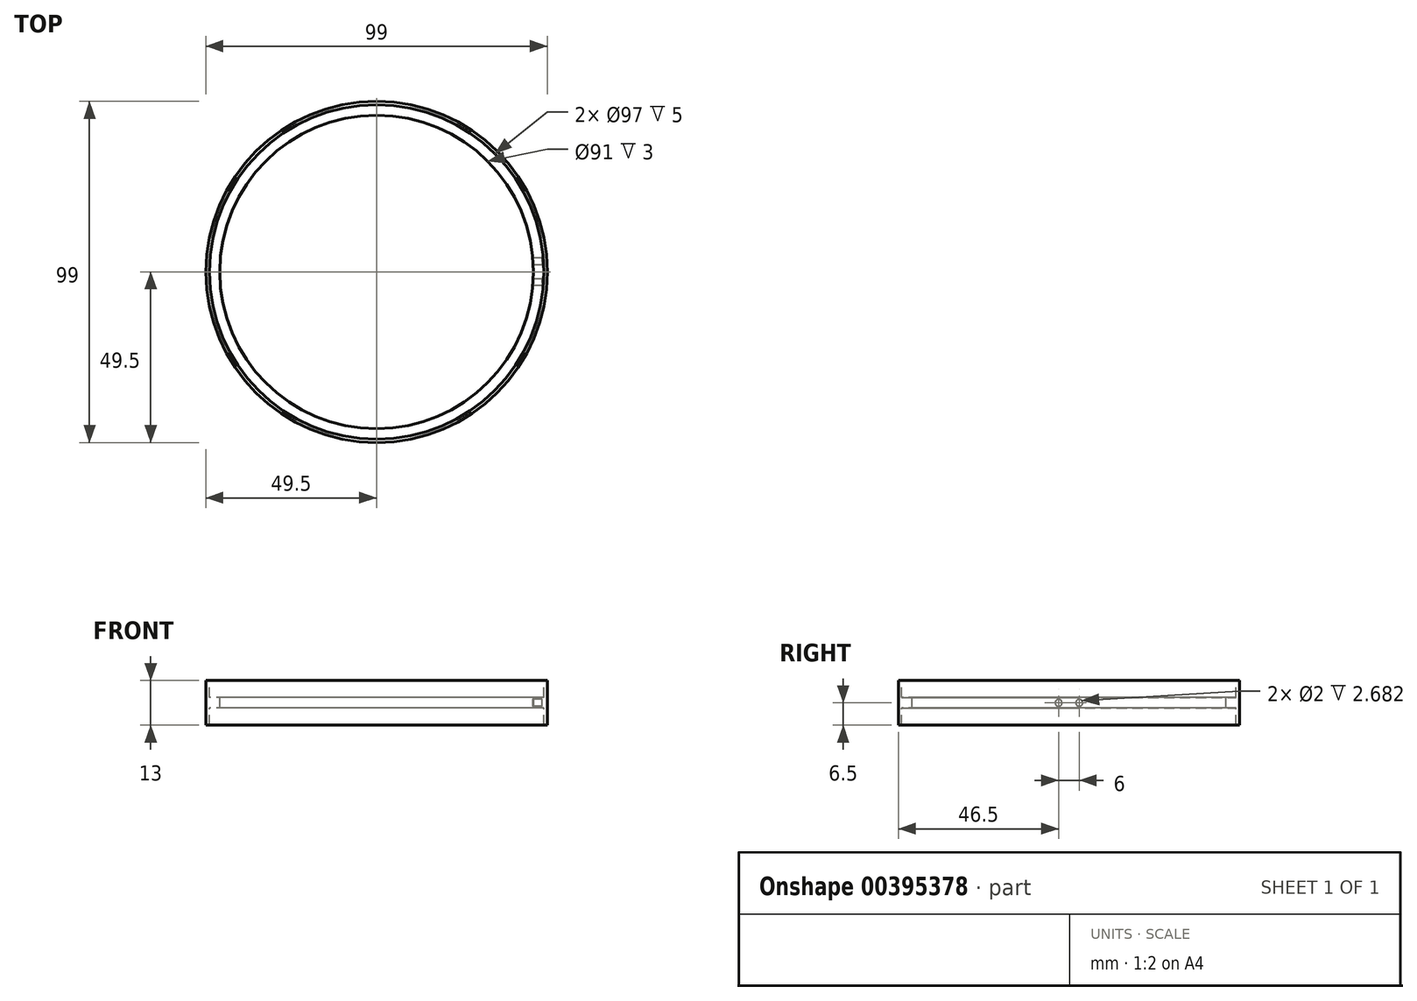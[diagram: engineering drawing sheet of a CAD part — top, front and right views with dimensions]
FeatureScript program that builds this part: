
annotation { "Feature Type Name" : "Feature", "Feature Type Description" : "" }
export const myFeature = defineFeature(function(context is Context, id is Id, definition is map)
    precondition{}
    {
        {
            var Q0;
            Q0=qCreatedBy(makeId("Front.planeOp"),FACE);
            var sketch = newSketch(context, id + "F0", { "sketchPlane" : qUnion([Q0])});
            skLineSegment(sketch, "E0", {"start": v(-49.5, 6.5) * mm, "end": v(-49.5, -6.5) * mm});
            skLineSegment(sketch, "E1", {"start": v(-49.5, -6.5) * mm, "end": v(-48.5, -6.5) * mm});
            skLineSegment(sketch, "E2", {"start": v(-48.5, -6.5) * mm, "end": v(-48.5, -1.5) * mm});
            skLineSegment(sketch, "E3", {"start": v(-48.5, -1.5) * mm, "end": v(-45.5, -1.5) * mm});
            skLineSegment(sketch, "E4", {"start": v(-45.5, -1.5) * mm, "end": v(-45.5, 1.5) * mm});
            skLineSegment(sketch, "E5", {"start": v(-45.5, 1.5) * mm, "end": v(-48.5, 1.5) * mm});
            skLineSegment(sketch, "E6", {"start": v(-48.5, 1.5) * mm, "end": v(-48.5, 6.5) * mm});
            skLineSegment(sketch, "E7", {"start": v(-48.5, 6.5) * mm, "end": v(-49.5, 6.5) * mm});
            skLineSegment(sketch, "E8", {"start": v(-48.5, 0) * mm, "end": v(0, 0) * mm});
            skLineSegment(sketch, "E9", {"start": v(0, 32.62) * mm, "end": v(0, -40.28) * mm});
            skSolve(sketch);
        }
        {
            var Q0;
            Q0=makeQuery(id+"F0.imprint","IMPRINT",FACE,{"disambiguationData":[TD([[makeQuery(id+"F0.imprint","IMPRINT",EDGE,{"derivedFrom":sQuery(id+"F0.wireOp",EDGE,"E0")}),1.0]])]});
            var Q1;
            Q1=sQuery(id+"F0.wireOp",EDGE,"E9");
            revolve(context, id + "F1", {"entities" : qUnion([Q0]), "axis" : qUnion([Q1]), "revolveType" : RevolveType.FULL});
        }
        {
            var Q0;
            Q0=qCreatedBy(makeId("Right.planeOp"),FACE);
            var sketch = newSketch(context, id + "F2", { "sketchPlane" : qUnion([Q0])});
            skLineSegment(sketch, "E10", {"start": v(0, 0) * mm, "end": v(-3, 0) * mm});
            skLineSegment(sketch, "E11", {"start": v(0, 0) * mm, "end": v(3, 0) * mm});
            skCircle(sketch, "E12", {"center": v(-3, 0) * mm, "radius": 1 * mm});
            skCircle(sketch, "E13", {"center": v(3, 0) * mm, "radius": 1 * mm});
            skSolve(sketch);
        }
        {
            var Q0;
            Q0 = qSketchRegion(id + "F2", true);
            extrude(context, id + "F3", {"entities" : qUnion([Q0]), "operationType" : NewBodyOperationType.REMOVE, "depth" : 48 * mm});
        }
        {
            var Q0;
            Q0=sQuery(id+"F2.wireOp",EDGE,"E12");
            var Q1;
            Q1=sQuery(id+"F2.wireOp",EDGE,"E13");
            extrude(context, id + "F4", {"bodyType" : ToolBodyType.SURFACE, "surfaceEntities" : qUnion([Q0, Q1]), "depth" : 60 * mm});
        }
    });
